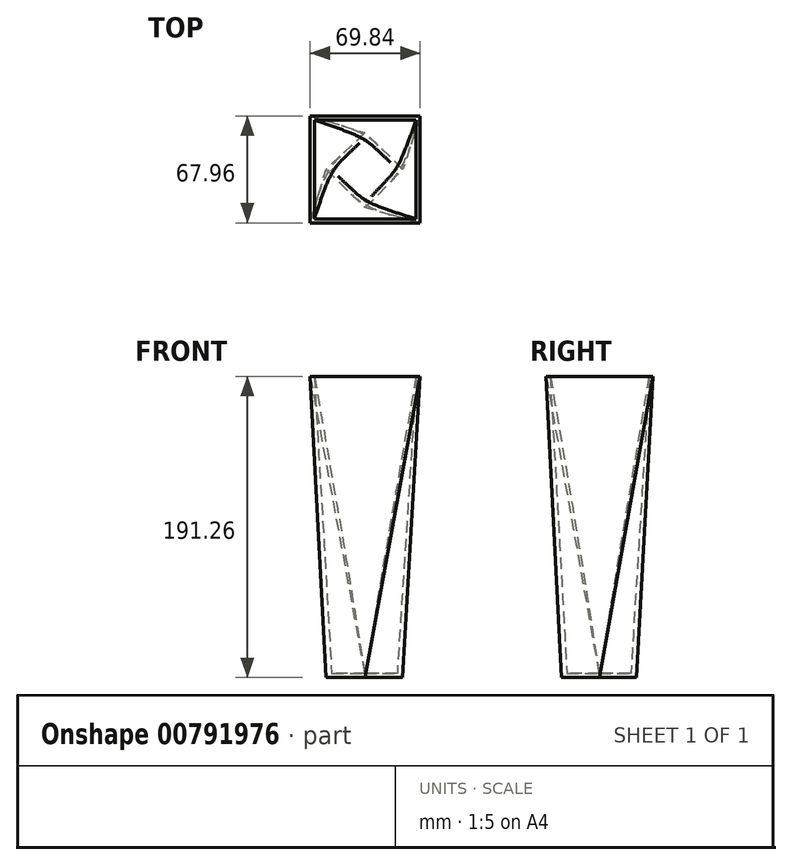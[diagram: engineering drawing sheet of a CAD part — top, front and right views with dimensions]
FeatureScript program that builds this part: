
annotation { "Feature Type Name" : "Feature", "Feature Type Description" : "" }
export const myFeature = defineFeature(function(context is Context, id is Id, definition is map)
    precondition{}
    {
        {
            var Q0;
            Q0=qCreatedBy(makeId("Top.planeOp"),FACE);
            cPlane(context, id + "F0", {"entities" : qUnion([Q0]), "cplaneType" : CPlaneType.OFFSET, "offset" : 127 * mm, "width" : 152.4 * mm, "height" : 152.4 * mm});
        }
        {
            var Q0;
            Q0=qCreatedBy(id+"F0.planeOp",FACE);
            var sketch = newSketch(context, id + "F1", { "sketchPlane" : qUnion([Q0])});
            skLineSegment(sketch, "E0.bottom", {"start": v(34.92, 33.98) * mm, "end": v(-34.92, 33.98) * mm});
            skLineSegment(sketch, "E0.top", {"start": v(34.92, -33.98) * mm, "end": v(-34.92, -33.98) * mm});
            skLineSegment(sketch, "E0.left", {"start": v(34.92, 33.98) * mm, "end": v(34.92, -33.98) * mm});
            skLineSegment(sketch, "E0.right", {"start": v(-34.92, 33.98) * mm, "end": v(-34.92, -33.98) * mm});
            skPoint(sketch, "E0.middle", {"position": v(0, 0) * mm});
            skSolve(sketch);
        }
        {
            var Q0;
            Q0=qCreatedBy(makeId("Top.planeOp"),FACE);
            cPlane(context, id + "F2", {"entities" : qUnion([Q0]), "cplaneType" : CPlaneType.OFFSET, "offset" : 64.26 * mm, "oppositeDirection" : true, "width" : 152.4 * mm, "height" : 152.4 * mm});
        }
        {
            var Q0;
            Q0=qCreatedBy(id+"F2.planeOp",FACE);
            var sketch = newSketch(context, id + "F3", { "sketchPlane" : qUnion([Q0])});
            skLineSegment(sketch, "E1", {"start": v(-24.89, 0) * mm, "end": v(0, -24.35) * mm});
            skLineSegment(sketch, "E2", {"start": v(0, -24.35) * mm, "end": v(23.82, 0) * mm});
            skLineSegment(sketch, "E3", {"start": v(23.82, 0) * mm, "end": v(0, 23.3) * mm});
            skLineSegment(sketch, "E4", {"start": v(0, 23.3) * mm, "end": v(-24.89, 0) * mm});
            skSolve(sketch);
        }
        {
            var Q0;
            Q0=makeQuery(id+"F1.imprint","IMPRINT",FACE,{"disambiguationData":[TD([[makeQuery(id+"F1.imprint","IMPRINT",EDGE,{"derivedFrom":sQuery(id+"F1.wireOp",EDGE,"E0.bottom")}),1.0]])]});
            var Q1;
            Q1=makeQuery(id+"F3.imprint","IMPRINT",FACE,{"disambiguationData":[TD([[makeQuery(id+"F3.imprint","IMPRINT",EDGE,{"derivedFrom":sQuery(id+"F3.wireOp",EDGE,"E1")}),1.0]])]});
            loft(context, id + "F4", {"sheetProfilesArray" : [{ "sheetProfileEntities" : qUnion([Q0]) }, { "sheetProfileEntities" : qUnion([Q1]) }]});
        }
        {
            var Q0;
            Q0=makeQuery(id+"F4.opLoft","CAP_FACE",FACE,{"disambiguationData":[OSD([makeQuery(id+"F1.imprint","IMPRINT",FACE,{"disambiguationData":[TD([[makeQuery(id+"F1.imprint","IMPRINT",EDGE,{"derivedFrom":sQuery(id+"F1.wireOp",EDGE,"E0.bottom")}),1.0]])]})])],"isStart":true});
            shell(context, id + "F5", {"entities" : qUnion([Q0]), "thickness" : 2.54 * mm});
        }
    });
